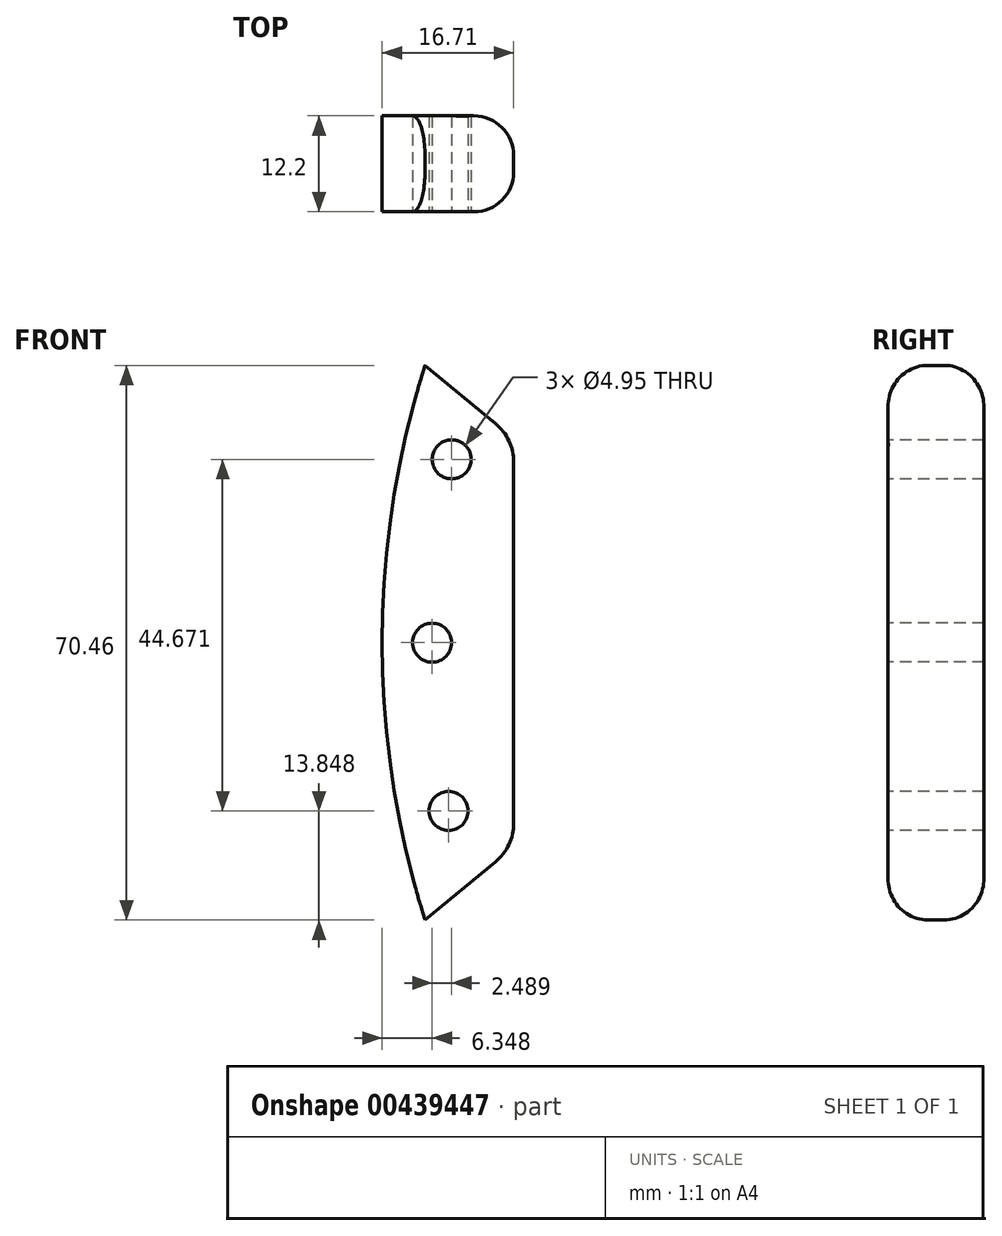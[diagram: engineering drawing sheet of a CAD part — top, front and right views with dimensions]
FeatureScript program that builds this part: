
annotation { "Feature Type Name" : "Feature", "Feature Type Description" : "" }
export const myFeature = defineFeature(function(context is Context, id is Id, definition is map)
    precondition{}
    {
        {
            var Q0;
            Q0=qCreatedBy(makeId("Front.planeOp"),FACE);
            var sketch = newSketch(context, id + "F0", { "sketchPlane" : qUnion([Q0])});
            skLineSegment(sketch, "E0", {"start": v(8.96, -32.3) * mm, "end": v(0, -39.7) * mm});
            skLineSegment(sketch, "E1", {"start": v(8.96, 23.36) * mm, "end": v(0, 30.76) * mm});
            skArc(sketch, "E2", {"start": v(0, 30.76) * mm, "mid": v(-5.45, -4.47) * mm, "end": v(0, -39.7) * mm});
            skLineSegment(sketch, "E3", {"start": v(11.26, 18.46) * mm, "end": v(11.26, -27.4) * mm});
            skPoint(sketch, "E4.visualSharp", {"position": v(11.26, 21.45) * mm});
            skArc(sketch, "E4.filletArc", {"start": v(11.26, 18.46) * mm, "mid": v(10.66, 21.17) * mm, "end": v(8.96, 23.36) * mm});
            skPoint(sketch, "E5.visualSharp", {"position": v(11.26, -30.4) * mm});
            skArc(sketch, "E5.filletArc", {"start": v(8.96, -32.3) * mm, "mid": v(10.66, -30.1) * mm, "end": v(11.26, -27.4) * mm});
            skSolve(sketch);
        }
        {
            var Q0;
            Q0=makeQuery(id+"F0.imprint","IMPRINT",FACE,{"disambiguationData":[TD([[makeQuery(id+"F0.imprint","IMPRINT",EDGE,{"derivedFrom":sQuery(id+"F0.wireOp",EDGE,"E0")}),-1.0]])]});
            extrude(context, id + "F1", {"entities" : qUnion([Q0]), "endBound" : BoundingType.SYMMETRIC, "depth" : 12.2 * mm});
        }
        {
            var Q0;
            Q0=makeQuery(id+"F1.opExtrude","CAP_FACE",FACE,{"disambiguationData":[OSD([sQuery(id+"F0.wireOp",EDGE,"E0"),sQuery(id+"F0.wireOp",EDGE,"E1"),sQuery(id+"F0.wireOp",EDGE,"kj8SREQD-eOZe-DUuQ-9VRb-ZCpHXTRVrNEz"),sQuery(id+"F0.wireOp",EDGE,"E2")])],"isStart":false});
            var sketch = newSketch(context, id + "F2", { "sketchPlane" : qUnion([Q0])});
            skPoint(sketch, "E6.centerSnap0", {"position": v(19.58, -4.47) * mm});
            skArc(sketch, "E7.0", {"start": v(6.05, 28.84) * mm, "mid": v(0.9, -4.47) * mm, "end": v(6.05, -37.78) * mm});
            skPoint(sketch, "E6.center.orphan", {"position": v(6.35, -4.47) * mm});
            skPoint(sketch, "E8.center.orphan", {"position": v(6.35, 18.82) * mm});
            skPoint(sketch, "E9.center.orphan", {"position": v(6.35, -25.85) * mm});
            skCircle(sketch, "E10", {"center": v(0.9, -4.47) * mm, "radius": 2.48 * mm});
            skCircle(sketch, "E11", {"center": v(3.39, 18.82) * mm, "radius": 2.48 * mm});
            skCircle(sketch, "E12", {"center": v(3, -25.85) * mm, "radius": 2.48 * mm});
            skSolve(sketch);
        }
        {
            var Q0;
            Q0 = qSketchRegion(id + "F2", true);
            extrude(context, id + "F3", {"entities" : qUnion([Q0]), "operationType" : NewBodyOperationType.REMOVE, "oppositeDirection" : true, "depth" : 25.4 * mm});
        }
        {
            var Q0;
            Q0=makeQuery(id+"F1.opExtrude","CAP_EDGE",EDGE,{"disambiguationData":[OSD([sQuery(id+"F0.wireOp",EDGE,"E3")])],"isStart":false});
            var Q1;
            Q1=makeQuery(id+"F1.opExtrude","CAP_EDGE",EDGE,{"disambiguationData":[OSD([sQuery(id+"F0.wireOp",EDGE,"E3")])],"isStart":true});
            fillet(context, id + "F4", {"entities" : qUnion([Q0, Q1]), "radius" : 5.08 * mm, "tangentPropagation" : true, "allowEdgeOverflow" : false});
        }
    });
